# Revit family: 505004 NANOSTEP LINEAR
name_source: partatom
category: Apparecchi per illuminazione
units: mm (PartAtom-declared; Revit-internal decimal feet)

## family parameters
Basato su piano di lavoro = No
Condiviso = Sì
Mantieni orientamento annotazione = No
Punto di calcolo locali = No
Quota connettore circolare = Usa diametro
Sempre verticale = Sì
Sorgente d'illuminazione = Sì
Taglio con vuoti quando caricato = No
Tipo di parte = Normale

## types (1)
- ALLOY
    Angolo inclinazione = 0.00°
    Available Optics = ASYMMETRICAL OVAL WIDE LIGHT DISTRIBUTION
    Colori = 4000°K   2700°K on request
    Filtro dei colori = 16777215
    Finish color = Alloy
    IK Rating = IK08
    IP Rating = IP68
    Ligjt Source = LED
    Material = Body and frontal cover in hard anodized aluminum
    Modello = NANOSTEP LINEAR
    Produttore = PUK
    Prospetto di default = 2023 mm
    Variazione temperatura colore lampada con luminosità attenuata = <Nessuno>
    Voltage = 700mA CC
    Wattage = 6W
